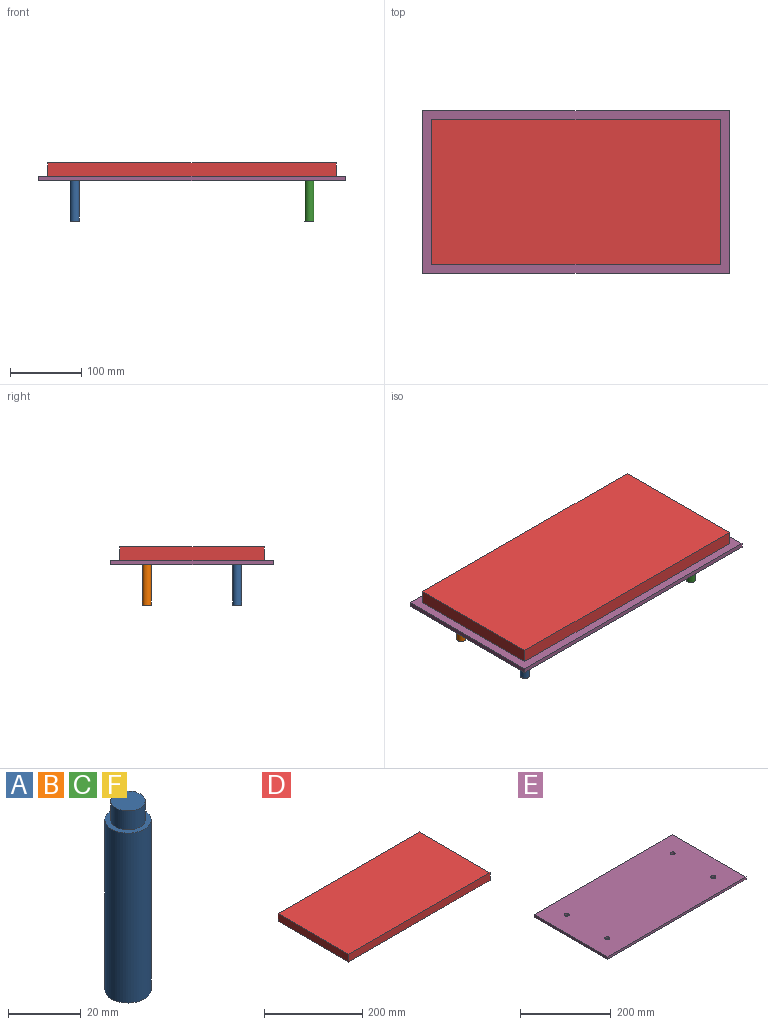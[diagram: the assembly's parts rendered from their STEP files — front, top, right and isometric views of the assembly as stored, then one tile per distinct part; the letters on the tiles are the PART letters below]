
ASSEMBLY  parts=6 mates=5
PART A: 5 faces, bbox 12.7x12.7x63.5 mm
  f0: cylinder r=6.35mm len=57.15mm, axis (0,0,1), area 2280.2mm2, adj f1,f2
  f1: plane 12.7x12.7mm, normal (0,0,-1), area 126.7mm2, adj f0
  f2: plane 12.7x12.7mm, normal (0,0,1), area 55.4mm2, adj f0,f3
  f3: cylinder r=4.76mm len=9.53mm, axis (0,0,-1), area 190mm2, adj f2,f4
  f4: plane 9.53x9.53mm, normal (0,0,1), area 71.3mm2, adj f3
PART B: same geometry as A
PART C: same geometry as A
PART D: 6 faces, bbox 406.4x203.2x19.1 mm
  f0: plane 203.2x19.05mm, normal (-1,0,0), area 3871mm2, adj f1,f3,f4,f5
  f1: plane 406.4x19.05mm, normal (0,-1,0), area 7741.9mm2, adj f0,f2,f4,f5
  f2: plane 203.2x19.05mm, normal (1,0,0), area 3871mm2, adj f1,f3,f4,f5
  f3: plane 406.4x19.05mm, normal (0,1,0), area 7741.9mm2, adj f0,f2,f4,f5
  f4: plane 406.4x203.2mm, normal (0,0,1), area 82580.5mm2, adj f0,f1,f2,f3
  f5: plane 406.4x203.2mm, normal (0,0,-1), area 82580.5mm2, adj f0,f1,f2,f3
PART E: 18 faces, bbox 431.8x228.6x6.4 mm
  f0: plane 228.6x6.35mm, normal (-1,0,0), area 1451.6mm2, adj f1,f3,f4,f5
  f1: plane 431.8x6.35mm, normal (0,-1,0), area 2741.9mm2, adj f0,f2,f4,f5
  f2: plane 228.6x6.35mm, normal (1,0,0), area 1451.6mm2, adj f1,f3,f4,f5
  f3: plane 431.8x6.35mm, normal (0,1,0), area 2741.9mm2, adj f0,f2,f4,f5
  f4: plane 431.8x228.6mm, normal (0,0,-1), area 97569.4mm2, adj f0,f1,f2,f3,f8,f11,f14,f17
  f5: plane 431.8x228.6mm, normal (0,0,1), area 98293.4mm2, adj f0,f1,f2,f3,f6,f9,f12,f15
  f6: cylinder r=5.75mm len=11.51mm, axis (0,0,-1), area 200.9mm2, adj f5,f7
  f7: plane 19.05x19.05mm, normal (0,0,-1), area 181mm2, adj f6,f8
  f8: cylinder r=9.53mm len=19.05mm, axis (0,0,-1), area 47.5mm2, adj f4,f7
  f9: cylinder r=5.75mm len=11.51mm, axis (0,0,-1), area 200.9mm2, adj f5,f10
  f10: plane 19.05x19.05mm, normal (0,0,-1), area 181mm2, adj f9,f11
  f11: cylinder r=9.53mm len=19.05mm, axis (0,0,-1), area 47.5mm2, adj f4,f10
  f12: cylinder r=5.75mm len=11.51mm, axis (0,0,-1), area 200.9mm2, adj f5,f13
  f13: plane 19.05x19.05mm, normal (0,0,-1), area 181mm2, adj f12,f14
  f14: cylinder r=9.53mm len=19.05mm, axis (0,0,-1), area 47.5mm2, adj f4,f13
  f15: cylinder r=5.75mm len=11.51mm, axis (0,0,-1), area 200.9mm2, adj f5,f16
  f16: plane 19.05x19.05mm, normal (0,0,-1), area 181mm2, adj f15,f17
  f17: cylinder r=9.53mm len=19.05mm, axis (0,0,-1), area 47.5mm2, adj f4,f16
PART F: same geometry as A
PLACE A t=(-165.1,-63.5,-5.56)mm
PLACE B t=(-165.1,63.5,-5.56)mm
PLACE C t=(165.1,-63.5,-5.56)mm
PLACE D at identity
PLACE E at identity fixed
PLACE F t=(165.1,63.5,-5.56)mm
MATE fastened D.f5 <-> E.f5  axis (0,0,-1) through (0,0,0)mm
MATE fastened C.f0 <-> E.f12  axis (0,0,1) through (165.1,-63.5,-5.56)mm
MATE fastened A.f0 <-> E.f9  axis (0,0,1) through (-165.1,-63.5,-5.56)mm
MATE fastened F.f0 <-> E.f15  axis (0,0,1) through (165.1,63.5,-5.56)mm
MATE fastened B.f0 <-> E.f6  axis (0,0,1) through (-165.1,63.5,-5.56)mm
